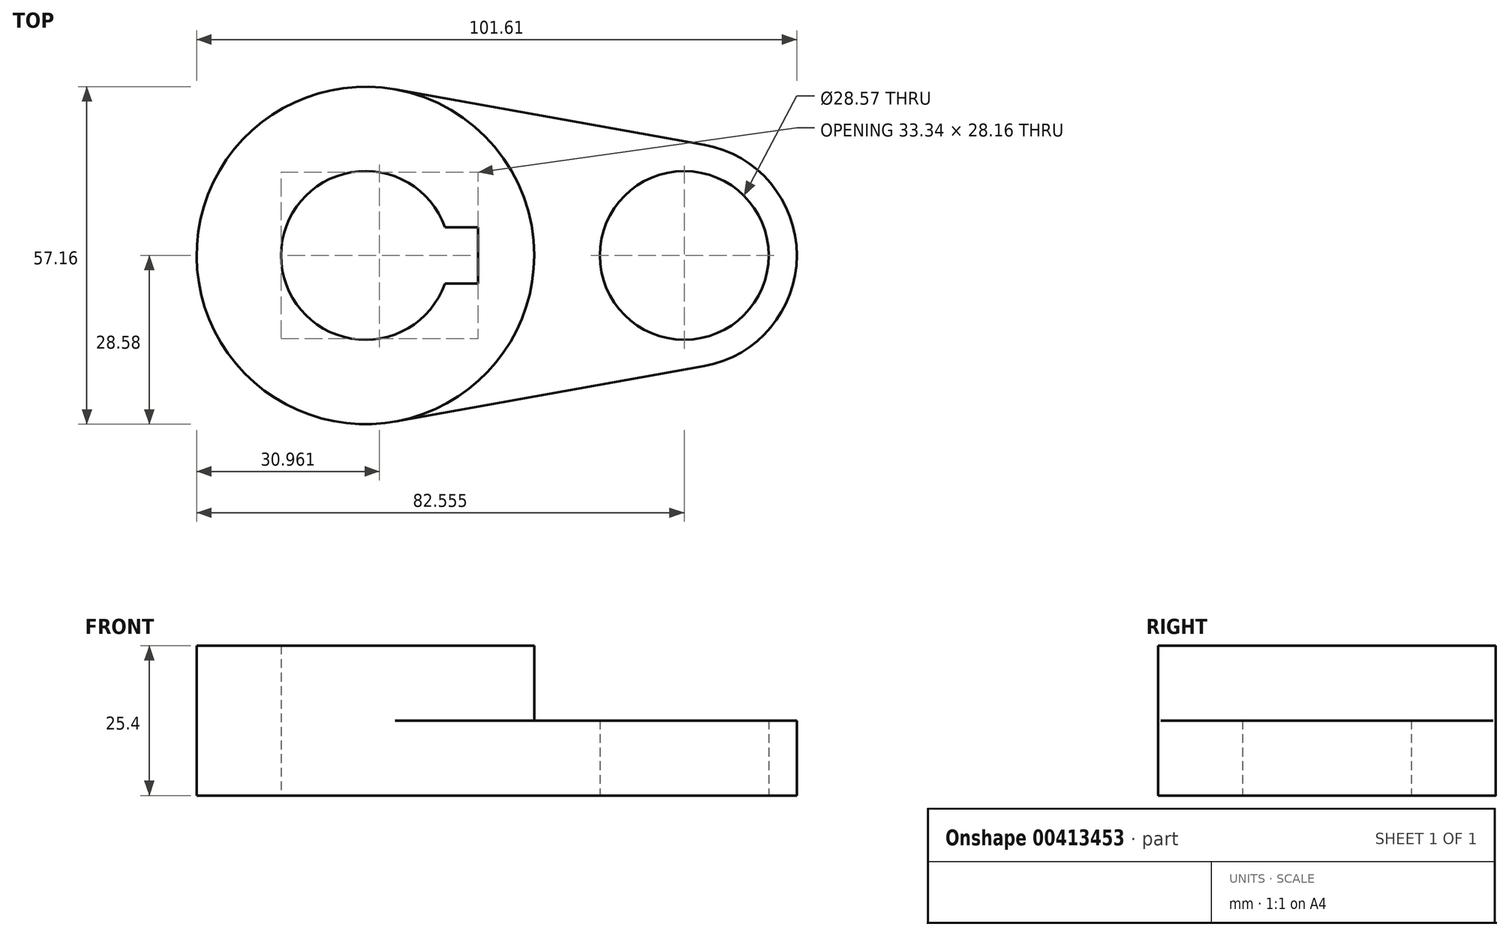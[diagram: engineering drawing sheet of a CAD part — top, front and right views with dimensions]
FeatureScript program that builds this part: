
annotation { "Feature Type Name" : "Feature", "Feature Type Description" : "" }
export const myFeature = defineFeature(function(context is Context, id is Id, definition is map)
    precondition{}
    {
        {
            var Q0;
            Q0=qCreatedBy(makeId("Top.planeOp"),FACE);
            var sketch = newSketch(context, id + "F0", { "sketchPlane" : qUnion([Q0])});
            skCircle(sketch, "E0", {"center": v(0, 0) * mm, "radius": 28.58 * mm});
            skCircle(sketch, "E1", {"center": v(53.98, 0) * mm, "radius": 19.05 * mm});
            skCircle(sketch, "E2", {"center": v(0, 0) * mm, "radius": 14.29 * mm});
            skCircle(sketch, "E3", {"center": v(53.98, 0) * mm, "radius": 14.29 * mm});
            skLineSegment(sketch, "E4.bottom", {"start": v(19.05, -4.76) * mm, "end": v(-19.05, -4.76) * mm});
            skLineSegment(sketch, "E4.top", {"start": v(19.05, 4.76) * mm, "end": v(-19.05, 4.76) * mm});
            skLineSegment(sketch, "E4.left", {"start": v(19.05, -4.76) * mm, "end": v(19.05, 4.76) * mm});
            skLineSegment(sketch, "E4.right", {"start": v(-19.05, -4.76) * mm, "end": v(-19.05, 4.76) * mm});
            skLineSegment(sketch, "E5", {"start": v(5.04, 28.13) * mm, "end": v(57.34, 18.75) * mm});
            skLineSegment(sketch, "E6", {"start": v(5.04, -28.13) * mm, "end": v(57.34, -18.75) * mm});
            skSolve(sketch);
        }
        {
            var Q0;
            {var subQ5=sQuery(id+"F0.wireOp",EDGE,"E4.right");Q0=makeQuery(id+"F0.imprint","IMPRINT",FACE,{"disambiguationData":[TD([[makeQuery(id+"F0.imprint","IMPRINT",EDGE,{"derivedFrom":subQ5}),-1.0]])]});}
            var Q1;
            {var subQ4=sQuery(id+"F0.wireOp",EDGE,"E4.left");Q1=makeQuery(id+"F0.imprint","IMPRINT",FACE,{"disambiguationData":[TD([[makeQuery(id+"F0.imprint","IMPRINT",EDGE,{"derivedFrom":subQ4}),-1.0]])]});}
            var Q2;
            {var subQ0=sQuery(id+"F0.wireOp",EDGE,"E5");Q2=makeQuery(id+"F0.imprint","IMPRINT",FACE,{"disambiguationData":[TD([[makeQuery(id+"F0.imprint","IMPRINT",EDGE,{"derivedFrom":subQ0}),-1.0]])]});}
            var Q3;
            Q3=makeQuery(id+"F0.imprint","IMPRINT",FACE,{"disambiguationData":[TD([[makeQuery(id+"F0.imprint","IMPRINT",EDGE,{"derivedFrom":sQuery(id+"F0.wireOp",EDGE,"E3")}),-1.0]])]});
            extrude(context, id + "F1", {"entities" : qUnion([Q0, Q1, Q2, Q3]), "depth" : 12.7 * mm});
        }
        {
            var Q0;
            {var subQ5=sQuery(id+"F0.wireOp",EDGE,"E4.right");Q0=makeQuery(id+"F0.imprint","IMPRINT",FACE,{"disambiguationData":[TD([[makeQuery(id+"F0.imprint","IMPRINT",EDGE,{"derivedFrom":subQ5}),-1.0]])]});}
            var Q1;
            {var subQ4=sQuery(id+"F0.wireOp",EDGE,"E4.left");Q1=makeQuery(id+"F0.imprint","IMPRINT",FACE,{"disambiguationData":[TD([[makeQuery(id+"F0.imprint","IMPRINT",EDGE,{"derivedFrom":subQ4}),-1.0]])]});}
            extrude(context, id + "F2", {"entities" : qUnion([Q0, Q1]), "operationType" : NewBodyOperationType.ADD, "depth" : 25.4 * mm});
        }
    });
